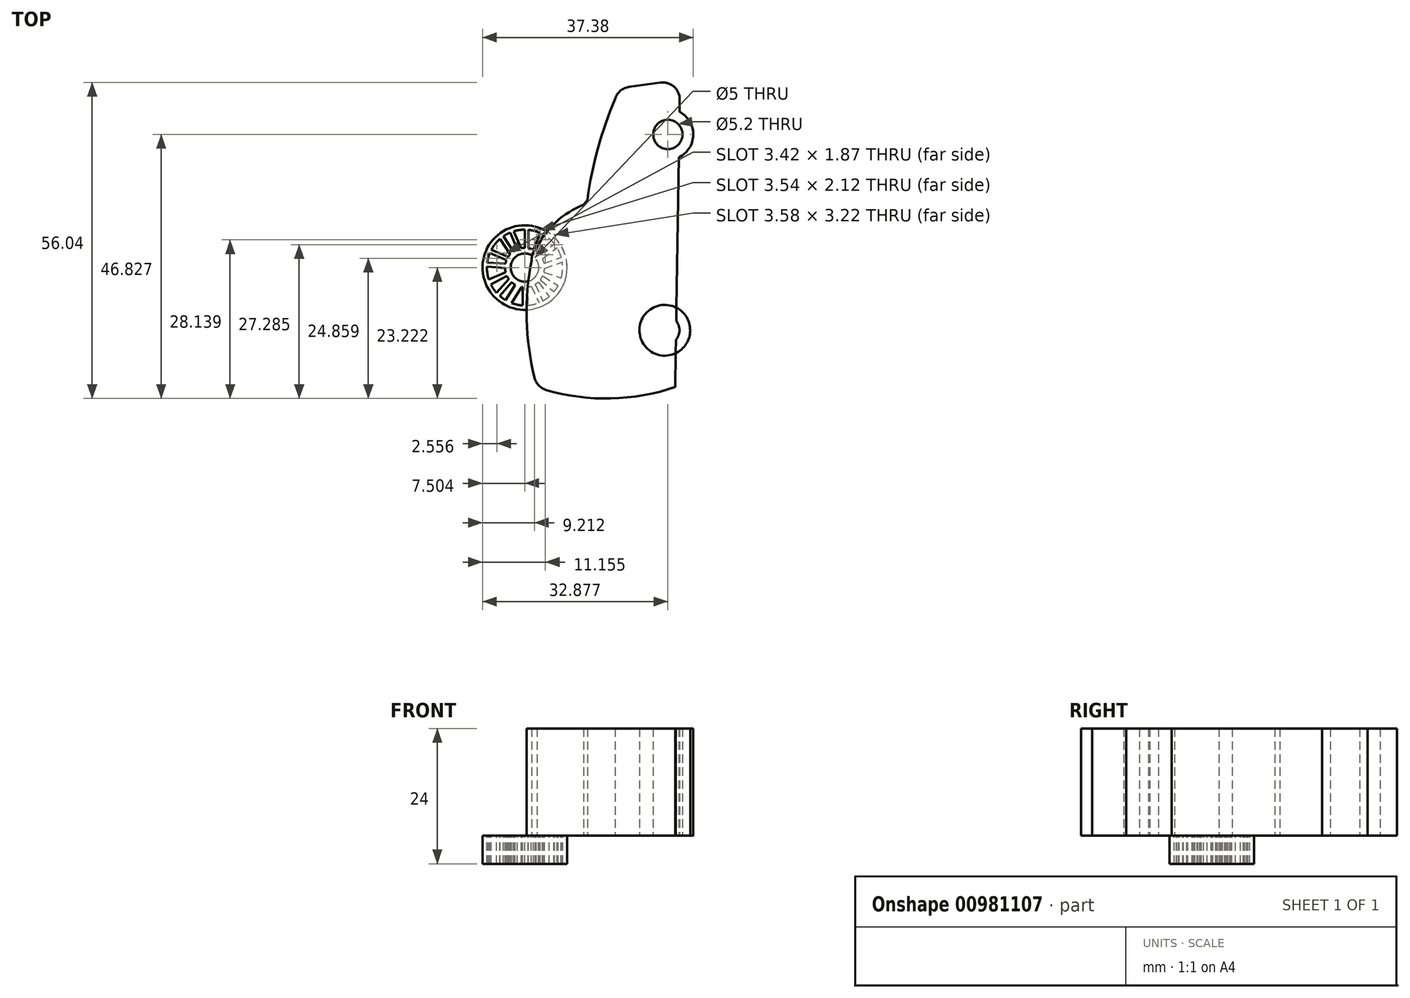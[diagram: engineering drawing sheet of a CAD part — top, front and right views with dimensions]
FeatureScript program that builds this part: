
annotation { "Feature Type Name" : "Feature", "Feature Type Description" : "" }
export const myFeature = defineFeature(function(context is Context, id is Id, definition is map)
    precondition{}
    {
        {
            var Q0;
            Q0=qCreatedBy(makeId("Top.planeOp"),FACE);
            var sketch = newSketch(context, id + "F0", { "sketchPlane" : qUnion([Q0])});
            skLineSegment(sketch, "E0", {"start": v(-24.06, 54.93) * mm, "end": v(-18.49, 55.69) * mm});
            skPoint(sketch, "E1.visualSharp", {"position": v(-26.02, 54.66) * mm});
            skArc(sketch, "E1.filletArc", {"start": v(-24.06, 54.93) * mm, "mid": v(-25.63, 54.22) * mm, "end": v(-26.55, 52.75) * mm});
            skLineSegment(sketch, "E2", {"start": v(-15.9, 1.7) * mm, "end": v(-15.08, 52.67) * mm});
            skArc(sketch, "E3.filletArc", {"start": v(-32.15, 34.03) * mm, "mid": v(-31.76, 34.46) * mm, "end": v(-31.46, 34.96) * mm});
            skPoint(sketch, "E4.visualSharp", {"position": v(-39.45, 25.51) * mm});
            skArc(sketch, "E4.filletArc", {"start": v(-40.37, 26.5) * mm, "mid": v(-41.12, 25.43) * mm, "end": v(-41.34, 24.15) * mm});
            skArc(sketch, "E5", {"start": v(-32.15, 34.03) * mm, "mid": v(-36.95, 31.02) * mm, "end": v(-40.37, 26.5) * mm});
            skArc(sketch, "E6", {"start": v(-26.55, 52.75) * mm, "mid": v(-29.6, 44.02) * mm, "end": v(-31.46, 34.96) * mm});
            skPoint(sketch, "E7.visualSharp", {"position": v(-15.03, 56.15) * mm});
            skArc(sketch, "E7.filletArc", {"start": v(-15.08, 52.67) * mm, "mid": v(-16.1, 54.96) * mm, "end": v(-18.49, 55.69) * mm});
            skArc(sketch, "E8", {"start": v(-41.34, 24.15) * mm, "mid": v(-42.22, 13.71) * mm, "end": v(-40.82, 3.34) * mm});
            skArc(sketch, "E9", {"start": v(-38.74, 1.18) * mm, "mid": v(-27.28, -0.32) * mm, "end": v(-15.9, 1.7) * mm});
            skPoint(sketch, "E10.visualSharp", {"position": v(-40.38, 1.7) * mm});
            skArc(sketch, "E10.filletArc", {"start": v(-40.82, 3.34) * mm, "mid": v(-40.07, 1.98) * mm, "end": v(-38.74, 1.18) * mm});
            skArc(sketch, "E11", {"start": v(-15.14, 11.88) * mm, "mid": v(-20.33, 11.77) * mm, "end": v(-15.14, 11.66) * mm});
            skCircle(sketch, "E12", {"center": v(-17.18, 46.5) * mm, "radius": 2.6 * mm});
            skLineSegment(sketch, "E13.trimOffspring", {"start": v(-15.14, 11.66) * mm, "end": v(-15.14, 11.88) * mm});
            skLineSegment(sketch, "E14", {"start": v(-17.73, 11.77) * mm, "end": v(-15.73, 11.74) * mm, "construction": true});
            skLineSegment(sketch, "E15", {"start": v(-17.18, 46.5) * mm, "end": v(-15.18, 46.47) * mm, "construction": true});
            skCircle(sketch, "E16", {"center": v(-17.73, 11.77) * mm, "radius": 4.5 * mm});
            skCircle(sketch, "E17", {"center": v(-17.18, 46.5) * mm, "radius": 4.5 * mm});
            skSolve(sketch);
        }
        {
            var Q0;
            {var subQ1=sQuery(id+"F0.wireOp",EDGE,"8QzBRkv9-rbrH-Hkkq-lZ2n-Ui9lD1EwF7Hd.bottom");Q0=makeQuery(id+"F0.imprint","IMPRINT",FACE,{"disambiguationData":[TD([[makeQuery(id+"F0.imprint","IMPRINT",EDGE,{"derivedFrom":subQ1}),-1.0]])]});}
            var Q1;
            {var subQ0=sQuery(id+"F0.wireOp",EDGE,"8QzBRkv9-rbrH-Hkkq-lZ2n-Ui9lD1EwF7Hd.right");var subQ1=sQuery(id+"F0.wireOp",EDGE,"8QzBRkv9-rbrH-Hkkq-lZ2n-Ui9lD1EwF7Hd.top");var subQ2=makeQuery(id+"F0.imprint","INTERSECT",VERTEX,{"derivedFrom":[subQ1,subQ0]});Q1=makeQuery(id+"F0.imprint","IMPRINT",FACE,{"disambiguationData":[TD([[makeQuery(id+"F0.imprint","IMPRINT",EDGE,{"disambiguationData":[TD([[subQ2,1.0]])],"derivedFrom":subQ1}),-1.0]])]});}
            var Q2;
            {var subQ0=sQuery(id+"F0.wireOp",EDGE,"8QzBRkv9-rbrH-Hkkq-lZ2n-Ui9lD1EwF7Hd.right");var subQ1=sQuery(id+"F0.wireOp",EDGE,"8QzBRkv9-rbrH-Hkkq-lZ2n-Ui9lD1EwF7Hd.top");var subQ2=makeQuery(id+"F0.imprint","INTERSECT",VERTEX,{"derivedFrom":[subQ1,subQ0]});Q2=makeQuery(id+"F0.imprint","IMPRINT",FACE,{"disambiguationData":[TD([[makeQuery(id+"F0.imprint","IMPRINT",EDGE,{"disambiguationData":[TD([[subQ2,1.0]])],"derivedFrom":subQ1}),1.0]])]});}
            var Q3;
            Q3=makeQuery(id+"F0.imprint","IMPRINT",FACE,{"disambiguationData":[TD([[makeQuery(id+"F0.imprint","IMPRINT",EDGE,{"derivedFrom":sQuery(id+"F0.wireOp",EDGE,"E0")}),-1.0]])]});
            var Q4;
            {var subQ5=sQuery(id+"F0.wireOp",EDGE,"A93q1p2C-ovS9-pCg6-Xjdj-ytGg551wDKpL.bottom");Q4=makeQuery(id+"F0.imprint","IMPRINT",FACE,{"disambiguationData":[TD([[makeQuery(id+"F0.imprint","IMPRINT",EDGE,{"derivedFrom":subQ5}),-1.0]])]});}
            var Q5;
            {var subQ4=sQuery(id+"F0.wireOp",EDGE,"eW0Uivwh-18e4-TSyW-KtAX-4BO7P9dj8XB2.bottom");Q5=makeQuery(id+"F0.imprint","IMPRINT",FACE,{"disambiguationData":[TD([[makeQuery(id+"F0.imprint","IMPRINT",EDGE,{"derivedFrom":subQ4}),-1.0]])]});}
            var Q6;
            {var subQ0=sQuery(id+"F0.wireOp",EDGE,"E17");var subQ1=sQuery(id+"F0.wireOp",EDGE,"E2");var subQ2=makeQuery(id+"F0.imprint","INTERSECT",VERTEX,{"disambiguationData":[OD(0.0)],"derivedFrom":[subQ1,subQ0]});Q6=makeQuery(id+"F0.imprint","IMPRINT",FACE,{"disambiguationData":[TD([[makeQuery(id+"F0.imprint","IMPRINT",EDGE,{"disambiguationData":[TD([[subQ2,-1.0]])],"derivedFrom":subQ1}),-1.0]])]});}
            var Q7;
            {var subQ0=sQuery(id+"F0.wireOp",EDGE,"E17");var subQ1=sQuery(id+"F0.wireOp",EDGE,"E2");var subQ2=makeQuery(id+"F0.imprint","INTERSECT",VERTEX,{"disambiguationData":[OD(0.0)],"derivedFrom":[subQ1,subQ0]});Q7=makeQuery(id+"F0.imprint","IMPRINT",FACE,{"disambiguationData":[TD([[makeQuery(id+"F0.imprint","IMPRINT",EDGE,{"disambiguationData":[TD([[subQ2,-1.0]])],"derivedFrom":subQ1}),1.0]])]});}
            var Q8;
            {var subQ0=sQuery(id+"F0.wireOp",EDGE,"E16");var subQ1=sQuery(id+"F0.wireOp",EDGE,"E2");var subQ2=makeQuery(id+"F0.imprint","INTERSECT",VERTEX,{"disambiguationData":[OD(0.0)],"derivedFrom":[subQ1,subQ0]});Q8=makeQuery(id+"F0.imprint","IMPRINT",FACE,{"disambiguationData":[TD([[makeQuery(id+"F0.imprint","IMPRINT",EDGE,{"disambiguationData":[TD([[subQ2,-1.0]])],"derivedFrom":subQ1}),1.0]])]});}
            var Q9;
            {var subQ0=sQuery(id+"F0.wireOp",EDGE,"E13.trimOffspring");Q9=makeQuery(id+"F0.imprint","IMPRINT",FACE,{"disambiguationData":[TD([[makeQuery(id+"F0.imprint","IMPRINT",EDGE,{"derivedFrom":subQ0}),-1.0]])]});}
            extrude(context, id + "F1", {"entities" : qUnion([Q0, Q1, Q2, Q3, Q4, Q5, Q6, Q7, Q8, Q9]), "depth" : 19 * mm, "offsetDistance" : 25 * mm});
        }
        {
            var Q0;
            Q0=qCreatedBy(makeId("Top.planeOp"),FACE);
            var sketch = newSketch(context, id + "F2", { "sketchPlane" : qUnion([Q0])});
            skCircle(sketch, "E18", {"center": v(-42.56, 22.9) * mm, "radius": 3.5 * mm});
            skCircle(sketch, "E19", {"center": v(-42.56, 22.9) * mm, "radius": 6.72 * mm});
            skLineSegment(sketch, "E20", {"start": v(-42.92, 19.41) * mm, "end": v(-42.92, 16.19) * mm});
            skLineSegment(sketch, "E21", {"start": v(-41.4, 19.59) * mm, "end": v(-40.03, 16.67) * mm});
            skLineSegment(sketch, "E22", {"start": v(-40.72, 19.91) * mm, "end": v(-39.35, 17) * mm});
            skPoint(sketch, "E22.startSnap0", {"position": v(-40.72, 18.13) * mm});
            skLineSegment(sketch, "E23", {"start": v(-41.98, 16.2) * mm, "end": v(-41.98, 19.44) * mm});
            skLineSegment(sketch, "E24", {"start": v(-44.27, 19.84) * mm, "end": v(-45.97, 17.1) * mm});
            skLineSegment(sketch, "E25", {"start": v(-44.88, 16.59) * mm, "end": v(-43.02, 19.59) * mm});
            skLineSegment(sketch, "E26", {"start": v(-44.88, 20.27) * mm, "end": v(-47, 17.86) * mm});
            skLineSegment(sketch, "E27", {"start": v(-47.55, 18.4) * mm, "end": v(-45.4, 20.84) * mm});
            skCircle(sketch, "E28", {"center": v(-42.56, 22.9) * mm, "radius": 7.5 * mm});
            skLineSegment(sketch, "E29", {"start": v(-45.71, 21.38) * mm, "end": v(-48.58, 19.91) * mm});
            skLineSegment(sketch, "E30", {"start": v(-45.95, 22.03) * mm, "end": v(-48.93, 20.79) * mm});
            skLineSegment(sketch, "E31", {"start": v(-46.05, 22.8) * mm, "end": v(-49.27, 23.06) * mm});
            skLineSegment(sketch, "E32", {"start": v(-45.98, 23.6) * mm, "end": v(-49.21, 23.78) * mm});
            skLineSegment(sketch, "E33", {"start": v(-45.49, 24.8) * mm, "end": v(-48.48, 26.05) * mm});
            skLineSegment(sketch, "E34", {"start": v(-45.17, 25.22) * mm, "end": v(-46.94, 27.98) * mm});
            skLineSegment(sketch, "E35", {"start": v(-44.6, 25.74) * mm, "end": v(-46.34, 28.44) * mm});
            skLineSegment(sketch, "E36", {"start": v(-43.89, 26.13) * mm, "end": v(-45.17, 29.08) * mm});
            skLineSegment(sketch, "E37", {"start": v(-43.2, 26.33) * mm, "end": v(-44.51, 29.32) * mm});
            skLineSegment(sketch, "E38", {"start": v(-42.56, 26.4) * mm, "end": v(-42.56, 29.6) * mm});
            skLineSegment(sketch, "E39", {"start": v(-41.9, 29.58) * mm, "end": v(-41.9, 26.33) * mm});
            skLineSegment(sketch, "E40", {"start": v(-41.02, 26.04) * mm, "end": v(-39.79, 29.01) * mm});
            skLineSegment(sketch, "E41", {"start": v(-40.52, 25.74) * mm, "end": v(-39.26, 28.75) * mm});
            skLineSegment(sketch, "E42", {"start": v(-39.9, 25.16) * mm, "end": v(-37.3, 27.07) * mm});
            skLineSegment(sketch, "E43", {"start": v(-39.44, 24.49) * mm, "end": v(-36.83, 26.4) * mm});
            skLineSegment(sketch, "E44", {"start": v(-39.13, 23.62) * mm, "end": v(-36.1, 24.71) * mm});
            skLineSegment(sketch, "E45", {"start": v(-39.06, 22.73) * mm, "end": v(-35.9, 23.86) * mm});
            skLineSegment(sketch, "E46", {"start": v(-39.16, 22.03) * mm, "end": v(-36.1, 21.04) * mm});
            skLineSegment(sketch, "E47", {"start": v(-39.4, 21.38) * mm, "end": v(-36.65, 19.68) * mm});
            skLineSegment(sketch, "E48", {"start": v(-39.8, 20.74) * mm, "end": v(-37.38, 18.6) * mm});
            skLineSegment(sketch, "E49", {"start": v(-40.15, 20.35) * mm, "end": v(-38.24, 17.75) * mm});
            skCircle(sketch, "E50", {"center": v(-42.56, 22.9) * mm, "radius": 2.5 * mm});
            skPoint(sketch, "E51.start.orphan", {"position": v(-44.51, 29.08) * mm});
            skLineSegment(sketch, "E52", {"start": v(-48.76, 25.46) * mm, "end": v(-45.8, 24.23) * mm});
            skSolve(sketch);
        }
        {
            var Q0;
            Q0 = qSketchRegion(id + "F2", true);
            var Q1;
            {var subQ0=sQuery(id+"F2.wireOp",EDGE,"E46");Q1=makeQuery(id+"F2.imprint","IMPRINT",FACE,{"disambiguationData":[TD([[makeQuery(id+"F2.imprint","IMPRINT",EDGE,{"derivedFrom":subQ0}),-1.0]])]});}
            var Q2;
            {var subQ0=sQuery(id+"F2.wireOp",EDGE,"E44");Q2=makeQuery(id+"F2.imprint","IMPRINT",FACE,{"disambiguationData":[TD([[makeQuery(id+"F2.imprint","IMPRINT",EDGE,{"derivedFrom":subQ0}),-1.0]])]});}
            var Q3;
            {var subQ0=sQuery(id+"F2.wireOp",EDGE,"E42");Q3=makeQuery(id+"F2.imprint","IMPRINT",FACE,{"disambiguationData":[TD([[makeQuery(id+"F2.imprint","IMPRINT",EDGE,{"derivedFrom":subQ0}),-1.0]])]});}
            var Q4;
            Q4=makeQuery(id+"F2.imprint","IMPRINT",FACE,{"disambiguationData":[TD([[makeQuery(id+"F2.imprint","IMPRINT",EDGE,{"derivedFrom":sQuery(id+"F2.wireOp",EDGE,"E50")}),-1.0]])]});
            var Q5;
            {var subQ0=sQuery(id+"F2.wireOp",EDGE,"E40");Q5=makeQuery(id+"F2.imprint","IMPRINT",FACE,{"disambiguationData":[TD([[makeQuery(id+"F2.imprint","IMPRINT",EDGE,{"derivedFrom":subQ0}),-1.0]])]});}
            var Q6;
            {var subQ0=sQuery(id+"F2.wireOp",EDGE,"E36");Q6=makeQuery(id+"F2.imprint","IMPRINT",FACE,{"disambiguationData":[TD([[makeQuery(id+"F2.imprint","IMPRINT",EDGE,{"derivedFrom":subQ0}),-1.0]])]});}
            var Q7;
            {var subQ0=sQuery(id+"F2.wireOp",EDGE,"E34");Q7=makeQuery(id+"F2.imprint","IMPRINT",FACE,{"disambiguationData":[TD([[makeQuery(id+"F2.imprint","IMPRINT",EDGE,{"derivedFrom":subQ0}),-1.0]])]});}
            var Q8;
            {var subQ0=sQuery(id+"F2.wireOp",EDGE,"bDMnpXBB-RnRU-z1Gd-g1rz-xBBI2HjO614n");Q8=makeQuery(id+"F2.imprint","IMPRINT",FACE,{"disambiguationData":[TD([[makeQuery(id+"F2.imprint","IMPRINT",EDGE,{"derivedFrom":subQ0}),-1.0]])]});}
            var Q9;
            {var subQ0=sQuery(id+"F2.wireOp",EDGE,"E31");Q9=makeQuery(id+"F2.imprint","IMPRINT",FACE,{"disambiguationData":[TD([[makeQuery(id+"F2.imprint","IMPRINT",EDGE,{"derivedFrom":subQ0}),-1.0]])]});}
            var Q10;
            {var subQ0=sQuery(id+"F2.wireOp",EDGE,"E29");Q10=makeQuery(id+"F2.imprint","IMPRINT",FACE,{"disambiguationData":[TD([[makeQuery(id+"F2.imprint","IMPRINT",EDGE,{"derivedFrom":subQ0}),-1.0]])]});}
            var Q11;
            {var subQ0=sQuery(id+"F2.wireOp",EDGE,"E26");Q11=makeQuery(id+"F2.imprint","IMPRINT",FACE,{"disambiguationData":[TD([[makeQuery(id+"F2.imprint","IMPRINT",EDGE,{"derivedFrom":subQ0}),-1.0]])]});}
            var Q12;
            {var subQ0=sQuery(id+"F2.wireOp",EDGE,"E24");Q12=makeQuery(id+"F2.imprint","IMPRINT",FACE,{"disambiguationData":[TD([[makeQuery(id+"F2.imprint","IMPRINT",EDGE,{"derivedFrom":subQ0}),1.0]])]});}
            var Q13;
            {var subQ0=sQuery(id+"F2.wireOp",EDGE,"E38");Q13=makeQuery(id+"F2.imprint","IMPRINT",FACE,{"disambiguationData":[TD([[makeQuery(id+"F2.imprint","IMPRINT",EDGE,{"derivedFrom":subQ0}),-1.0]])]});}
            var Q14;
            {var subQ0=sQuery(id+"F2.wireOp",EDGE,"E20");Q14=makeQuery(id+"F2.imprint","IMPRINT",FACE,{"disambiguationData":[TD([[makeQuery(id+"F2.imprint","IMPRINT",EDGE,{"derivedFrom":subQ0}),1.0]])]});}
            var Q15;
            {var subQ0=sQuery(id+"F2.wireOp",EDGE,"E21");Q15=makeQuery(id+"F2.imprint","IMPRINT",FACE,{"disambiguationData":[TD([[makeQuery(id+"F2.imprint","IMPRINT",EDGE,{"derivedFrom":subQ0}),1.0]])]});}
            var Q16;
            {var subQ0=sQuery(id+"F2.wireOp",EDGE,"E48");Q16=makeQuery(id+"F2.imprint","IMPRINT",FACE,{"disambiguationData":[TD([[makeQuery(id+"F2.imprint","IMPRINT",EDGE,{"derivedFrom":subQ0}),-1.0]])]});}
            var Q17;
            {var subQ0=sQuery(id+"F2.wireOp",EDGE,"E33");Q17=makeQuery(id+"F2.imprint","IMPRINT",FACE,{"disambiguationData":[TD([[makeQuery(id+"F2.imprint","IMPRINT",EDGE,{"derivedFrom":subQ0}),1.0]])]});}
            extrude(context, id + "F3", {"entities" : qUnion([Q0, Q1, Q2, Q3, Q4, Q5, Q6, Q7, Q8, Q9, Q10, Q11, Q12, Q13, Q14, Q15, Q16, Q17]), "oppositeDirection" : true, "depth" : 5 * mm, "offsetDistance" : 25 * mm});
        }
    });
